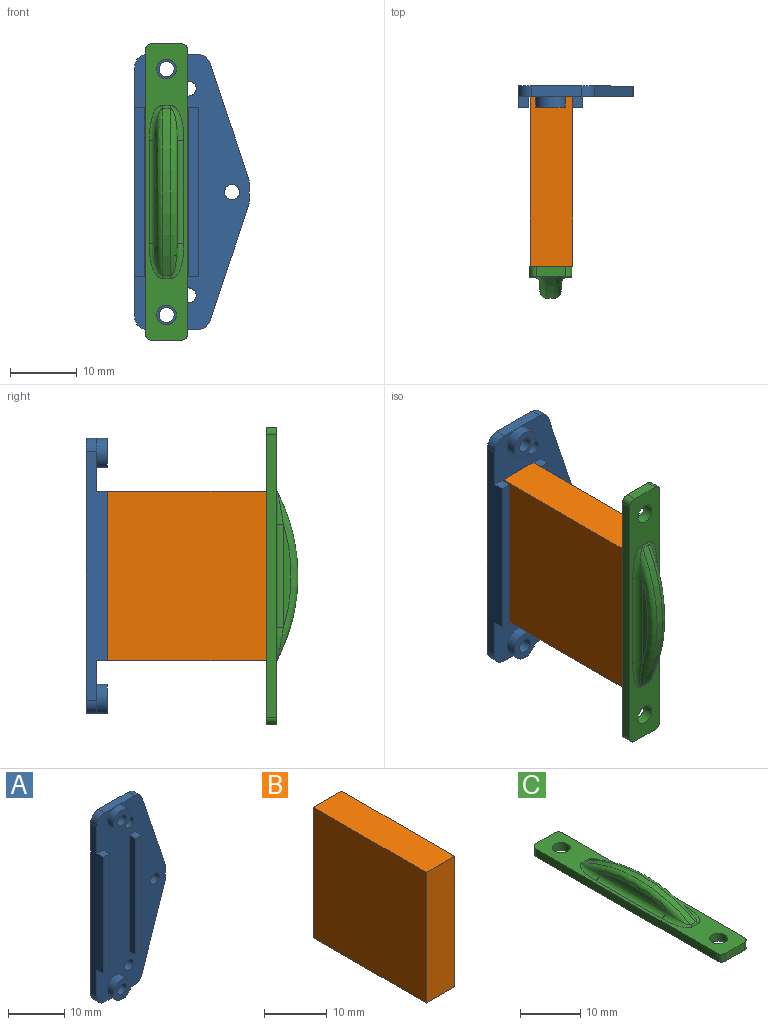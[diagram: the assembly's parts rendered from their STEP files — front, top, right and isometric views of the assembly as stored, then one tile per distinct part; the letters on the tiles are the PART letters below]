
ASSEMBLY  parts=3 mates=5
PART A: 36 faces, bbox 17.2x3.2x41.3 mm
  f0: plane 41.28x17.23mm, normal (0,-1,0), area 469.5mm2, adj f1,f2,f3,f4,f5,f8,f9,f10
  f1: plane 37.28x3.18mm, normal (-1,0,0), area 99.5mm2, adj f0,f12,f13,f14,f16,f30,f35
  f2: plane 7.43x1.59mm, normal (0,0,-1), area 11.8mm2, adj f0,f12,f29,f30,f31
  f3: plane 17.37x5.79mm, normal (0.95,0,-0.32), area 29.1mm2, adj f0,f12,f31,f32
  f4: plane 2.53x1.59mm, normal (1,0,0), area 4mm2, adj f0,f12,f32,f33
  f5: plane 17.37x5.79mm, normal (0.95,0,0.32), area 29.1mm2, adj f0,f12,f33,f34
  f6: cylinder r=1.13mm len=3.18mm, axis (0,-1,0), area 22.5mm2, adj f12,f28
  f7: cylinder r=1.13mm len=3.18mm, axis (0,-1,0), area 22.5mm2, adj f12,f25
  f8: cylinder r=1.12mm len=2.25mm, axis (0,-1,0), area 11.2mm2, adj f0,f12
  f9: cylinder r=1.12mm len=2.25mm, axis (0,-1,0), area 11.2mm2, adj f0,f12
  f10: cylinder r=1.12mm len=2.25mm, axis (0,-1,0), area 11.2mm2, adj f0,f12
  f11: plane 7.43x1.59mm, normal (0,0,1), area 11.8mm2, adj f0,f12,f22,f34,f35
  f12: plane 41.28x17.23mm, normal (0,1,0), area 567.5mm2, adj f1,f2,f3,f4,f5,f6,f7,f8
  f13: plane 1.59x1.5mm, normal (0,0,1), area 2.4mm2, adj f0,f1,f15,f16
  f14: plane 1.59x1.5mm, normal (0,0,-1), area 2.4mm2, adj f0,f1,f15,f16
  f15: plane 25.4x1.59mm, normal (1,0,0), area 40.3mm2, adj f0,f13,f14,f16
  f16: plane 25.4x1.5mm, normal (0,-1,0), area 38.1mm2, adj f1,f13,f14,f15
  f17: plane 1.59x1.5mm, normal (0,0,1), area 2.4mm2, adj f0,f18,f20,f21
  f18: plane 25.4x1.59mm, normal (-1,0,0), area 40.3mm2, adj f0,f17,f19,f21
  f19: plane 1.59x1.5mm, normal (0,0,-1), area 2.4mm2, adj f0,f18,f20,f21
  f20: plane 25.4x1.59mm, normal (1,0,0), area 40.3mm2, adj f0,f17,f19,f21
  f21: plane 25.4x1.5mm, normal (0,-1,0), area 38.1mm2, adj f17,f18,f19,f20
  f22: plane 0.37x0.01mm, normal (0,1,0), area 0mm2, adj f11,f24
  f23: cylinder r=2.65mm len=1.59mm, axis (0,1,0), area 3.4mm2, adj f0,f24,f25
  f24: cylinder r=2.23mm len=4.46mm, axis (0,1,0), area 18.8mm2, adj f0,f22,f23,f25
  f25: plane 4.46x4.46mm, normal (0,-1,0), area 10.9mm2, adj f7,f23,f24
  f26: cylinder r=2.23mm len=4.46mm, axis (0,1,0), area 18.8mm2, adj f0,f27,f28,f29
  f27: cylinder r=2.65mm len=1.59mm, axis (0,1,0), area 3.4mm2, adj f0,f26,f28
  f28: plane 4.46x4.46mm, normal (0,-1,0), area 10.9mm2, adj f6,f26,f27
  f29: plane 0.37x0.01mm, normal (0,1,0), area 0mm2, adj f2,f26
  f30: cylinder r=2mm len=2mm, axis (0,1,0), area 5mm2, adj f0,f1,f2,f12
  f31: cylinder r=2mm len=1.9mm, axis (0,-1,0), area 4mm2, adj f0,f2,f3,f12
  f32: cylinder r=2mm len=1.59mm, axis (0,-1,0), area 1mm2, adj f0,f3,f4,f12
  f33: cylinder r=2mm len=1.59mm, axis (0,1,0), area 1mm2, adj f0,f4,f5,f12
  f34: cylinder r=2mm len=1.9mm, axis (0,-1,0), area 4mm2, adj f0,f5,f11,f12
  f35: cylinder r=2mm len=2mm, axis (0,-1,0), area 5mm2, adj f0,f1,f11,f12
PART B: 6 faces, bbox 6.4x25.4x25.4 mm
  f0: plane 25.4x6.35mm, normal (0,1,0), area 161.3mm2, adj f1,f3,f4,f5
  f1: plane 25.4x6.35mm, normal (0,0,1), area 161.3mm2, adj f0,f2,f4,f5
  f2: plane 25.4x6.35mm, normal (0,-1,0), area 161.3mm2, adj f1,f3,f4,f5
  f3: plane 25.4x6.35mm, normal (0,0,-1), area 161.3mm2, adj f0,f2,f4,f5
  f4: plane 25.4x25.4mm, normal (1,0,0), area 645.2mm2, adj f0,f1,f2,f3
  f5: plane 25.4x25.4mm, normal (-1,0,0), area 645.2mm2, adj f0,f1,f2,f3
PART C: 25 faces, bbox 6.4x44.5x7 mm
  f0: plane 4.35x1.59mm, normal (0,1,0), area 6.9mm2, adj f6,f7,f21,f24
  f1: plane 42.45x1.59mm, normal (-1,0,0), area 67.4mm2, adj f6,f7,f21,f22
  f2: plane 4.35x1.59mm, normal (0,-1,0), area 6.9mm2, adj f6,f7,f22,f23
  f3: cylinder r=1.47mm len=2.95mm, axis (0,0,1), area 14.7mm2, adj f6,f7
  f4: cylinder r=1.47mm len=2.95mm, axis (0,0,1), area 14.7mm2, adj f6,f7
  f5: plane 42.45x1.59mm, normal (1,0,0), area 67.4mm2, adj f6,f7,f23,f24
  f6: plane 44.45x6.35mm, normal (0,0,-1), area 267.8mm2, adj f0,f1,f2,f3,f4,f5,f21,f22
  f7: plane 44.45x6.35mm, normal (0,0,1), area 141.7mm2, adj f0,f1,f2,f3,f4,f5,f11,f12
  f8: cylinder r=26.99mm len=24.97mm, axis (-1,0,0), area 30.5mm2, adj f11,f14,f17,f20
  f9: plane 15.45x1.18mm, normal (1,0,0), area 12.2mm2, adj f14,f15
  f10: plane 15.45x1.18mm, normal (-1,0,0), area 12.2mm2, adj f16,f17
  f11: cylinder r=1mm len=1.18mm, axis (-1,0,0), area 0.6mm2, adj f7,f8,f12,f13
  f12: bspline ~5.25x2.05mm, area 5.8mm2, adj f7,f11,f14,f15
  f13: bspline ~7.89x2.11mm, area 5.8mm2, adj f7,f11,f16,f17
  f14: torus R=25.99mm, axis (1,0,0), area 35.4mm2, adj f8,f9,f12,f18
  f15: cylinder r=1mm len=15.45mm, axis (0,-1,0), area 24.3mm2, adj f7,f9,f12,f18
  f16: cylinder r=1mm len=15.45mm, axis (0,1,0), area 24.3mm2, adj f7,f10,f13,f19
  f17: torus R=25.99mm, axis (1,0,0), area 35.4mm2, adj f8,f10,f13,f19
  f18: bspline ~7.89x2.11mm, area 5.8mm2, adj f7,f14,f15,f20
  f19: bspline ~5.25x2.05mm, area 5.8mm2, adj f7,f16,f17,f20
  f20: cylinder r=1mm len=1.18mm, axis (-1,0,0), area 0.6mm2, adj f7,f8,f18,f19
  f21: cylinder r=1mm len=1.59mm, axis (0,0,-1), area 2.5mm2, adj f0,f1,f6,f7
  f22: cylinder r=1mm len=1.59mm, axis (0,0,1), area 2.5mm2, adj f1,f2,f6,f7
  f23: cylinder r=1mm len=1.59mm, axis (0,0,-1), area 2.5mm2, adj f2,f5,f6,f7
  f24: cylinder r=1mm len=1.59mm, axis (0,0,1), area 2.5mm2, adj f0,f5,f6,f7
PLACE A t=(0.83,-1.59,0)mm
PLACE B t=(-5.52,-14.29,0)mm
PLACE C rot(axis=(1,0,0),90deg) t=(-2.47,-28.58,0)mm
MATE cylindrical A.f6 <-> C.f4  axis (0,-1,0) through (-2.47,-3.17,-18.42)mm
MATE planar B.f0 <-> A.f0  axis (0,1,0) through (-2.34,-1.59,0)mm
MATE planar B.f4 <-> A.f18  axis (1,0,0) through (0.83,-14.29,0)mm
MATE planar C.f6 <-> B.f2  axis (0,1,0) through (-2.47,-26.99,0)mm
MATE cylindrical A.f7 <-> C.f3  axis (0,-1,0) through (-2.47,-1.59,18.42)mm
